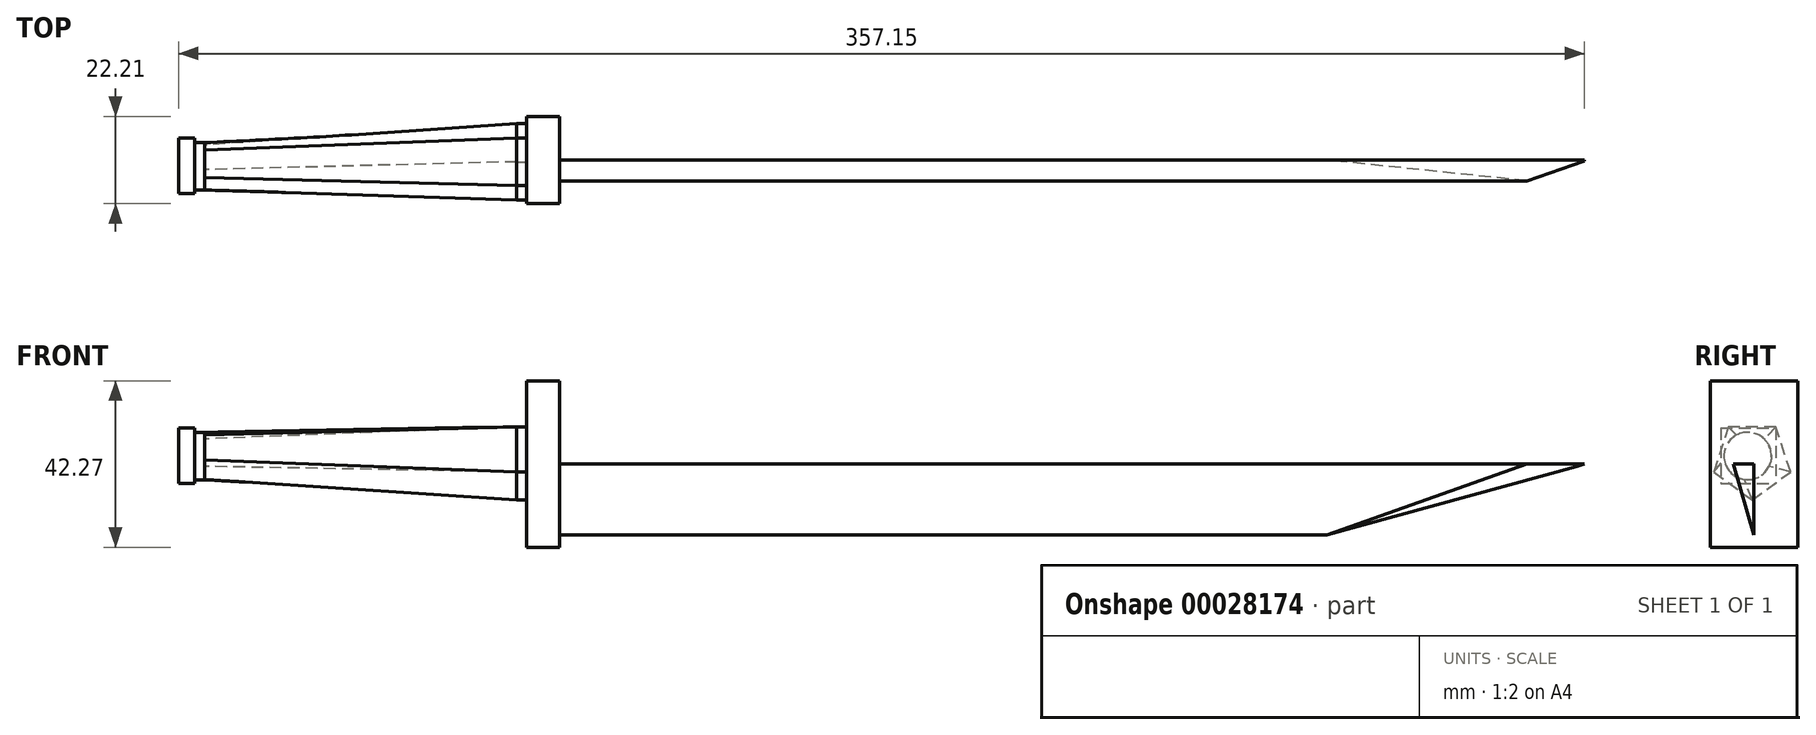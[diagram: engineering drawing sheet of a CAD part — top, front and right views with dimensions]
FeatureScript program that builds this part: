
annotation { "Feature Type Name" : "Feature", "Feature Type Description" : "" }
export const myFeature = defineFeature(function(context is Context, id is Id, definition is map)
    precondition{}
    {
        {
            var Q0;
            Q0=qCreatedBy(makeId("Front.planeOp"),FACE);
            var sketch = newSketch(context, id + "F0", { "sketchPlane" : qUnion([Q0])});
            skLineSegment(sketch, "E0", {"start": v(0, 0) * mm, "end": v(266.29, 0) * mm});
            skLineSegment(sketch, "E1", {"start": v(266.29, 0) * mm, "end": v(0, 0) * mm});
            skLineSegment(sketch, "E2", {"start": v(0, 0) * mm, "end": v(-1029.94, 0) * mm});
            skLineSegment(sketch, "E3", {"start": v(266.29, 0) * mm, "end": v(266.29, 4.84) * mm});
            skLineSegment(sketch, "E4", {"start": v(-92.75, 0) * mm, "end": v(-92.75, 42.27) * mm});
            skLineSegment(sketch, "E5", {"start": v(-92.75, 42.27) * mm, "end": v(-96.8, 42.27) * mm});
            skLineSegment(sketch, "E6", {"start": v(-96.8, 42.27) * mm, "end": v(-96.8, 0) * mm});
            skLineSegment(sketch, "E7", {"start": v(27.67, 0) * mm, "end": v(27.67, 39.4) * mm});
            skLineSegment(sketch, "E8", {"start": v(27.67, 39.4) * mm, "end": v(36.01, 39.4) * mm});
            skLineSegment(sketch, "E9", {"start": v(36.01, 39.4) * mm, "end": v(36.01, 0) * mm});
            skSolve(sketch);
        }
        {
            var Q0;
            {var subQ1=sQuery(id+"F0.wireOp",EDGE,"E4");Q0=makeQuery(id+"F0.imprint","IMPRINT",FACE,{"disambiguationData":[TD([[makeQuery(id+"F0.imprint","IMPRINT",EDGE,{"derivedFrom":subQ1}),1.0]])]});}
            extrude(context, id + "F1", {"entities" : qUnion([Q0]), "depth" : 25.4 * mm});
        }
        {
            var Q0;
            Q0=qCreatedBy(makeId("Front.planeOp"),FACE);
            var sketch = newSketch(context, id + "F2", { "sketchPlane" : qUnion([Q0])});
            skLineSegment(sketch, "E10", {"start": v(0, 0) * mm, "end": v(0, 42.27) * mm});
            skLineSegment(sketch, "E11", {"start": v(0, 42.27) * mm, "end": v(-8.34, 42.27) * mm});
            skLineSegment(sketch, "E12", {"start": v(-8.34, 42.27) * mm, "end": v(-8.34, 0) * mm});
            skLineSegment(sketch, "E13", {"start": v(-8.34, 0) * mm, "end": v(0, 0) * mm});
            skSolve(sketch);
        }
        {
            var Q0;
            Q0=makeQuery(id+"F2.imprint","IMPRINT",FACE,{"disambiguationData":[TD([[makeQuery(id+"F2.imprint","IMPRINT",EDGE,{"derivedFrom":sQuery(id+"F2.wireOp",EDGE,"E10")}),1.0]])]});
            extrude(context, id + "F3", {"entities" : qUnion([Q0]), "depth" : 25.4 * mm});
        }
        {
            var Q0;
            Q0=makeQuery(id+"F3.opExtrude","SWEPT_FACE",FACE,{"disambiguationData":[OSD([sQuery(id+"F2.wireOp",EDGE,"E12")])]});
            var sketch = newSketch(context, id + "F4", { "sketchPlane" : qUnion([Q0])});
            skCircle(sketch, "E14.cCircle", {"center": v(12.22, 22.3) * mm, "radius": 8.31 * mm, "construction": true});
            skLineSegment(sketch, "E14.0", {"start": v(6.18, 30.6) * mm, "end": v(18.26, 30.6) * mm});
            skLineSegment(sketch, "E14.1", {"start": v(18.26, 30.6) * mm, "end": v(22, 19.12) * mm});
            skLineSegment(sketch, "E14.2", {"start": v(22, 19.12) * mm, "end": v(12.22, 12.02) * mm});
            skLineSegment(sketch, "E14.3", {"start": v(12.22, 12.02) * mm, "end": v(2.45, 19.12) * mm});
            skLineSegment(sketch, "E14.4", {"start": v(2.45, 19.12) * mm, "end": v(6.18, 30.6) * mm});
            skPoint(sketch, "E14.0.midPoint", {"position": v(12.22, 30.6) * mm});
            skSolve(sketch);
        }
        {
            var Q0;
            Q0=makeQuery(id+"F1.opExtrude","SWEPT_FACE",FACE,{"disambiguationData":[OSD([sQuery(id+"F0.wireOp",EDGE,"E4")])]});
            var sketch = newSketch(context, id + "F5", { "sketchPlane" : qUnion([Q0])});
            skCircle(sketch, "E15", {"center": v(-13.37, 23.17) * mm, "radius": 6.02 * mm});
            skSolve(sketch);
        }
        {
            var Q0;
            Q0=makeQuery(id+"F5.imprint","IMPRINT",FACE,{"disambiguationData":[TD([[makeQuery(id+"F5.imprint","IMPRINT",EDGE,{"derivedFrom":sQuery(id+"F5.wireOp",EDGE,"E15")}),1.0]])]});
            extrude(context, id + "F6", {"entities" : qUnion([Q0]), "operationType" : NewBodyOperationType.ADD, "depth" : 2.54 * mm});
        }
        {
            var Q0;
            Q0=makeQuery(id+"F4.imprint","IMPRINT",FACE,{"disambiguationData":[TD([[makeQuery(id+"F4.imprint","IMPRINT",EDGE,{"derivedFrom":sQuery(id+"F4.wireOp",EDGE,"E14.0")}),-1.0]])]});
            extrude(context, id + "F7", {"entities" : qUnion([Q0]), "operationType" : NewBodyOperationType.ADD, "depth" : 2.54 * mm});
        }
        {
            var Q1;
            Q1=makeQuery(id+"F7.opExtrude","CAP_FACE",FACE,{"disambiguationData":[OSD([sQuery(id+"F4.wireOp",EDGE,"E14.0"),sQuery(id+"F4.wireOp",EDGE,"E14.1"),sQuery(id+"F4.wireOp",EDGE,"E14.2"),sQuery(id+"F4.wireOp",EDGE,"E14.3"),sQuery(id+"F4.wireOp",EDGE,"E14.4")])],"isStart":false});
            var Q2;
            Q2=makeQuery(id+"F6.opExtrude","CAP_FACE",FACE,{"disambiguationData":[OSD([sQuery(id+"F5.wireOp",EDGE,"E15")])],"isStart":false});
            loft(context, id + "F8", {"operationType" : NewBodyOperationType.ADD, "sheetProfilesArray" : [{ "sheetProfileEntities" : qUnion([Q1]) }, { "sheetProfileEntities" : qUnion([Q2]) }]});
        }
        {
            var Q0;
            Q0=makeQuery(id+"F1.opExtrude","SWEPT_FACE",FACE,{"disambiguationData":[OSD([sQuery(id+"F0.wireOp",EDGE,"E5")])]});
            extrude(context, id + "F9", {"entities" : qUnion([Q0]), "operationType" : NewBodyOperationType.REMOVE, "oppositeDirection" : true, "depth" : 12 * mm});
        }
        {
            var Q0;
            Q0=makeQuery(id+"F1.opExtrude","CAP_FACE",FACE,{"disambiguationData":[OSD([sQuery(id+"F0.wireOp",EDGE,"E2"),sQuery(id+"F0.wireOp",EDGE,"E4"),sQuery(id+"F0.wireOp",EDGE,"E5"),sQuery(id+"F0.wireOp",EDGE,"E6")])],"isStart":true});
            extrude(context, id + "F10", {"entities" : qUnion([Q0]), "operationType" : NewBodyOperationType.REMOVE, "oppositeDirection" : true, "depth" : 6.22 * mm});
        }
        {
            var Q0;
            Q0=makeQuery(id+"F1.opExtrude","SWEPT_FACE",FACE,{"disambiguationData":[OSD([sQuery(id+"F0.wireOp",EDGE,"E2")])]});
            extrude(context, id + "F11", {"entities" : qUnion([Q0]), "operationType" : NewBodyOperationType.REMOVE, "oppositeDirection" : true, "depth" : 16.26 * mm});
        }
        {
            var Q0;
            Q0=makeQuery(id+"F1.opExtrude","CAP_FACE",FACE,{"disambiguationData":[OSD([sQuery(id+"F0.wireOp",EDGE,"E2"),sQuery(id+"F0.wireOp",EDGE,"E4"),sQuery(id+"F0.wireOp",EDGE,"E5"),sQuery(id+"F0.wireOp",EDGE,"E6")])],"isStart":false});
            extrude(context, id + "F12", {"entities" : qUnion([Q0]), "operationType" : NewBodyOperationType.REMOVE, "oppositeDirection" : true, "depth" : 5.17 * mm});
        }
        {
            var Q0;
            Q0=makeQuery(id+"F3.opExtrude","CAP_FACE",FACE,{"disambiguationData":[OSD([sQuery(id+"F2.wireOp",EDGE,"E10"),sQuery(id+"F2.wireOp",EDGE,"E11"),sQuery(id+"F2.wireOp",EDGE,"E12"),sQuery(id+"F2.wireOp",EDGE,"E13")])],"isStart":false});
            extrude(context, id + "F13", {"entities" : qUnion([Q0]), "operationType" : NewBodyOperationType.REMOVE, "oppositeDirection" : true, "depth" : 2.53 * mm});
        }
        {
            var Q0;
            Q0=makeQuery(id+"F3.opExtrude","CAP_FACE",FACE,{"disambiguationData":[OSD([sQuery(id+"F2.wireOp",EDGE,"E10"),sQuery(id+"F2.wireOp",EDGE,"E11"),sQuery(id+"F2.wireOp",EDGE,"E12"),sQuery(id+"F2.wireOp",EDGE,"E13")])],"isStart":true});
            extrude(context, id + "F14", {"entities" : qUnion([Q0]), "operationType" : NewBodyOperationType.REMOVE, "oppositeDirection" : true, "depth" : 0.66 * mm});
        }
        {
            var Q0;
            Q0=makeQuery(id+"F3.opExtrude","SWEPT_FACE",FACE,{"disambiguationData":[OSD([sQuery(id+"F2.wireOp",EDGE,"E10")])]});
            var sketch = newSketch(context, id + "F15", { "sketchPlane" : qUnion([Q0])});
            skLineSegment(sketch, "E16", {"start": v(-11.77, 0) * mm, "end": v(-11.77, 42.27) * mm});
            skLineSegment(sketch, "E17", {"start": v(-11.77, 21.13) * mm, "end": v(-17.28, 21.13) * mm});
            skLineSegment(sketch, "E18", {"start": v(-17.28, 21.13) * mm, "end": v(-17.28, 2.82) * mm});
            skLineSegment(sketch, "E19", {"start": v(-17.28, 2.82) * mm, "end": v(-11.77, 2.82) * mm});
            skSolve(sketch);
        }
        {
            var Q0;
            {var subQ1=sQuery(id+"F15.wireOp",EDGE,"E17");Q0=makeQuery(id+"F15.imprint","IMPRINT",FACE,{"disambiguationData":[TD([[makeQuery(id+"F15.imprint","IMPRINT",EDGE,{"derivedFrom":subQ1}),1.0]])]});}
            extrude(context, id + "F16", {"entities" : qUnion([Q0]), "operationType" : NewBodyOperationType.ADD, "depth" : 260.35 * mm});
        }
        {
            var Q0;
            Q0=makeQuery(id+"F16.opExtrude","SWEPT_FACE",FACE,{"disambiguationData":[OSD([sQuery(id+"F15.wireOp",EDGE,"E18")])]});
            var sketch = newSketch(context, id + "F17", { "sketchPlane" : qUnion([Q0])});
            skLineSegment(sketch, "E20", {"start": v(260.35, 21.13) * mm, "end": v(208.9, 2.82) * mm});
            skSolve(sketch);
        }
        {
            var Q0;
            {var subQ2=sQuery(id+"F17.wireOp",EDGE,"E20");Q0=makeQuery(id+"F17.imprint","IMPRINT",FACE,{"disambiguationData":[TD([[makeQuery(id+"F17.imprint","IMPRINT",EDGE,{"derivedFrom":subQ2}),1.0]])]});}
            extrude(context, id + "F18", {"entities" : qUnion([Q0]), "operationType" : NewBodyOperationType.REMOVE, "oppositeDirection" : true, "depth" : 25.4 * mm});
        }
        {
            var Q0;
            Q0=makeQuery(id+"F16.opExtrude","SWEPT_EDGE",EDGE,{"disambiguationData":[OSD([sQuery(id+"F15.wireOp",EDGE,"E18"),sQuery(id+"F15.wireOp",EDGE,"E19")])]});
            chamfer(context, id + "F19", {"entities" : qUnion([Q0]), "chamferType" : ChamferType.TWO_OFFSETS, "width1" : 5.6 * mm, "oppositeDirection" : false, "width2" : 19.05 * mm, "tangentPropagation" : true});
        }
        {
            var Q0;
            Q0=makeQuery(id+"F19.opChamfer","BLEND_EDGE",EDGE,{"blendedFrom":[makeQuery(id+"F16.opExtrude","SWEPT_EDGE",EDGE,{"disambiguationData":[OSD([sQuery(id+"F15.wireOp",EDGE,"E18"),sQuery(id+"F15.wireOp",EDGE,"E19")])]}),makeQuery(id+"F18.boolean.opBoolean","COPY",FACE,{"derivedFrom":makeQuery(id+"F18.opExtrude","SWEPT_FACE",FACE,{"disambiguationData":[OSD([sQuery(id+"F17.wireOp",EDGE,"E20")])]})})],"blendedInto":[makeQuery(id+"F18.boolean.opBoolean","COPY",FACE,{"derivedFrom":makeQuery(id+"F18.opExtrude","SWEPT_FACE",FACE,{"disambiguationData":[OSD([sQuery(id+"F17.wireOp",EDGE,"E20")])]})})]});
            chamfer(context, id + "F20", {"entities" : qUnion([Q0]), "chamferType" : ChamferType.TWO_OFFSETS, "width1" : 5.08 * mm, "oppositeDirection" : false, "width2" : 5.08 * mm, "tangentPropagation" : true});
        }
    });
